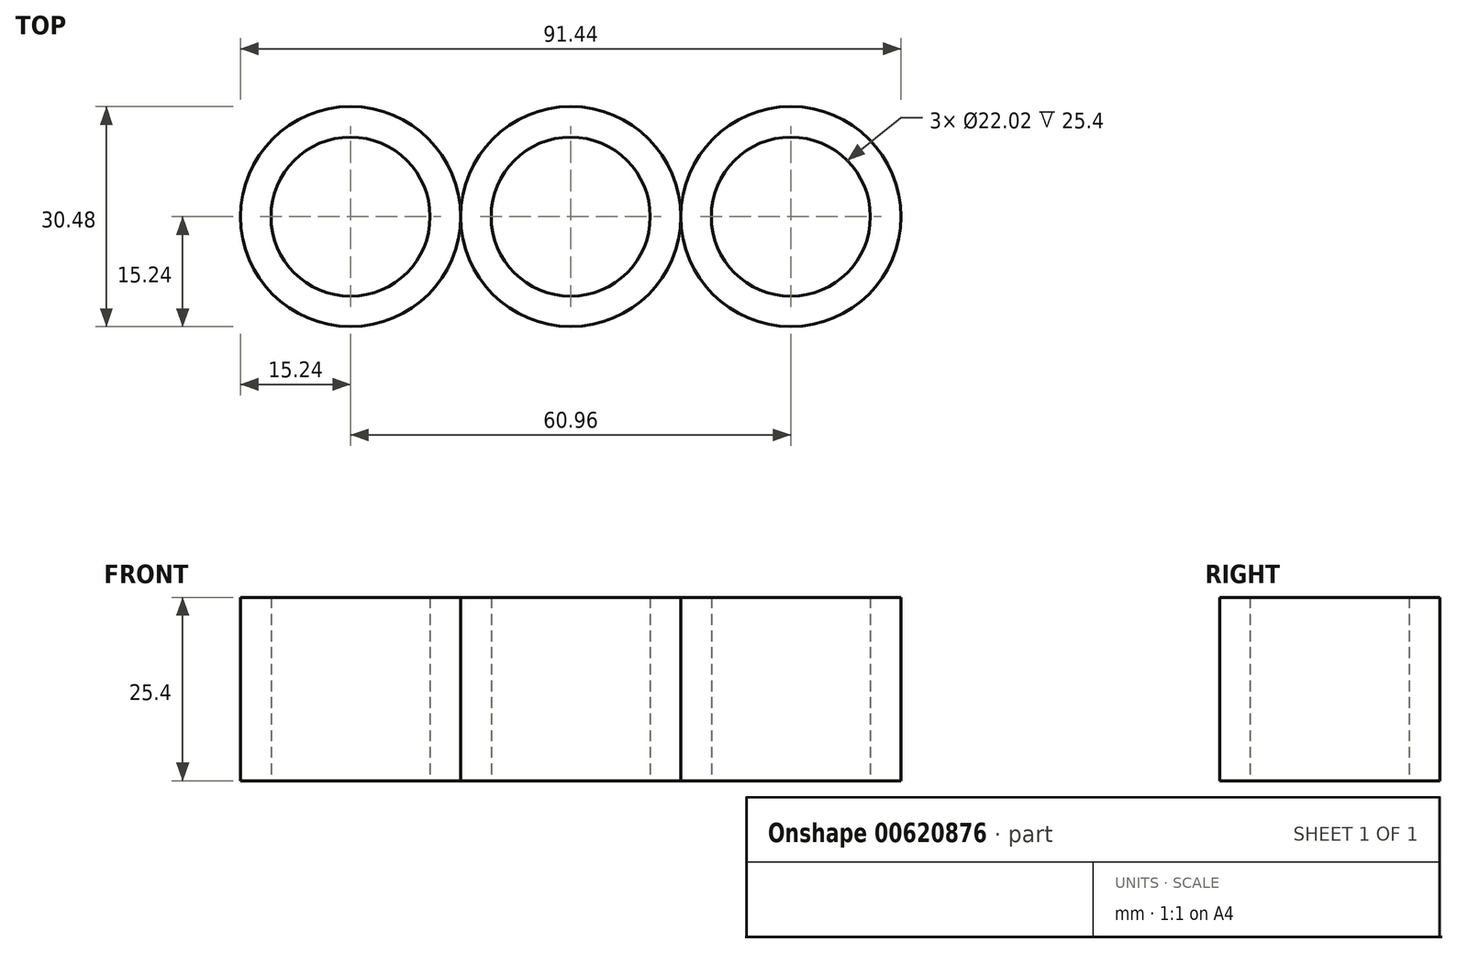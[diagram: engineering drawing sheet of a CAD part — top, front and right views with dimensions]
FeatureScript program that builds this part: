
annotation { "Feature Type Name" : "Feature", "Feature Type Description" : "" }
export const myFeature = defineFeature(function(context is Context, id is Id, definition is map)
    precondition{}
    {
        {
            var Q0;
            Q0=qCreatedBy(makeId("Top.planeOp"),FACE);
            var sketch = newSketch(context, id + "F0", { "sketchPlane" : qUnion([Q0])});
            skCircle(sketch, "E0", {"center": v(0, 0) * mm, "radius": 11.01 * mm});
            skLineSegment(sketch, "E1", {"start": v(0, 0) * mm, "end": v(30.48, 0) * mm});
            skLineSegment(sketch, "E2", {"start": v(0, 0) * mm, "end": v(-30.48, 0) * mm});
            skCircle(sketch, "E3", {"center": v(-30.48, 0) * mm, "radius": 11.01 * mm});
            skCircle(sketch, "E4", {"center": v(30.48, 0) * mm, "radius": 11.01 * mm});
            skCircle(sketch, "E5", {"center": v(-30.48, 0) * mm, "radius": 15.24 * mm});
            skCircle(sketch, "E6", {"center": v(0, 0) * mm, "radius": 15.24 * mm});
            skCircle(sketch, "E7", {"center": v(30.48, 0) * mm, "radius": 15.24 * mm});
            skSolve(sketch);
        }
        {
            var Q0;
            Q0 = qSketchRegion(id + "F0", true);
            extrude(context, id + "F1", {"entities" : qUnion([Q0]), "depth" : 25.4 * mm, "offsetDistance" : 25.4 * mm});
        }
    });
